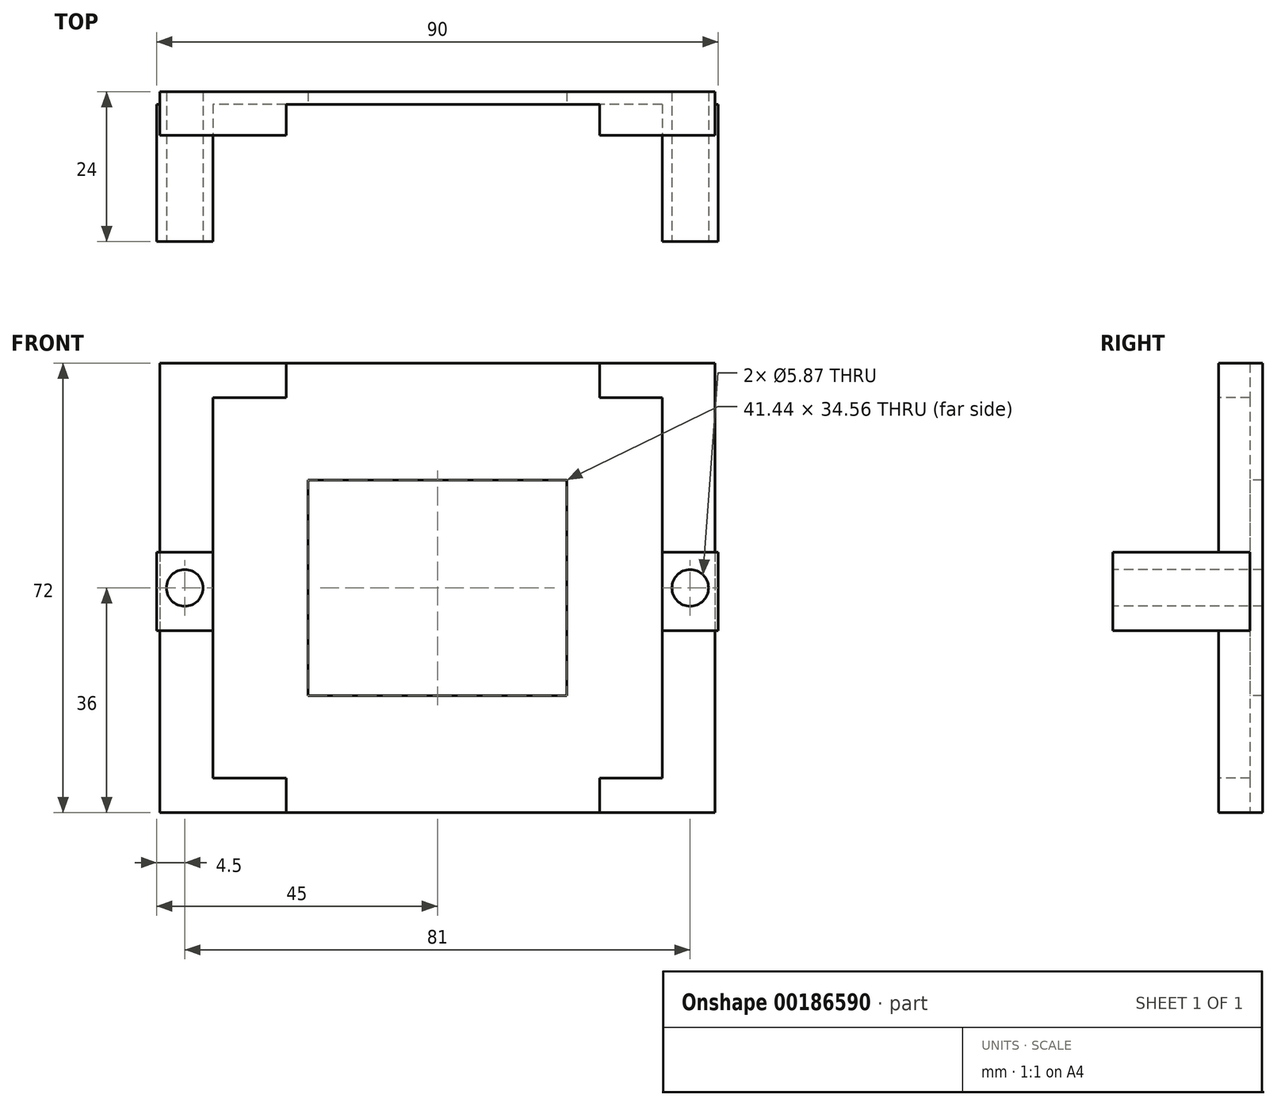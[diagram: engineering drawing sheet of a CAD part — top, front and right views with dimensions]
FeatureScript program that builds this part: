
annotation { "Feature Type Name" : "Feature", "Feature Type Description" : "" }
export const myFeature = defineFeature(function(context is Context, id is Id, definition is map)
    precondition{}
    {
        {
            var Q0;
            Q0=qCreatedBy(makeId("Front.planeOp"),FACE);
            var sketch = newSketch(context, id + "F0", { "sketchPlane" : qUnion([Q0])});
            skPoint(sketch, "E0.middle", {"position": v(0, 0) * mm});
            skLineSegment(sketch, "E1.bottom", {"start": v(44.5, 36) * mm, "end": v(-44.5, 36) * mm});
            skLineSegment(sketch, "E1.top", {"start": v(44.5, -36) * mm, "end": v(-44.5, -36) * mm});
            skLineSegment(sketch, "E1.left", {"start": v(44.5, 36) * mm, "end": v(44.5, -36) * mm});
            skLineSegment(sketch, "E1.right", {"start": v(-44.5, 36) * mm, "end": v(-44.5, -36) * mm});
            skSolve(sketch);
        }
        {
            var Q0;
            Q0 = qSketchRegion(id + "F0", true);
            extrude(context, id + "F1", {"entities" : qUnion([Q0]), "depth" : 7 * mm});
        }
        {
            var Q0;
            Q0=makeQuery(id+"F1.opExtrude","CAP_FACE",FACE,{"disambiguationData":[OSD([sQuery(id+"F0.wireOp",EDGE,"E1.bottom"),sQuery(id+"F0.wireOp",EDGE,"E1.top"),sQuery(id+"F0.wireOp",EDGE,"E1.left"),sQuery(id+"F0.wireOp",EDGE,"E1.right")])],"isStart":false});
            var sketch = newSketch(context, id + "F2", { "sketchPlane" : qUnion([Q0])});
            skLineSegment(sketch, "E2.bottom", {"start": v(36, 30.5) * mm, "end": v(-36, 30.5) * mm});
            skLineSegment(sketch, "E2.top", {"start": v(36, -30.5) * mm, "end": v(-36, -30.5) * mm});
            skLineSegment(sketch, "E2.left", {"start": v(36, 30.5) * mm, "end": v(36, -30.5) * mm});
            skLineSegment(sketch, "E2.right", {"start": v(-36, 30.5) * mm, "end": v(-36, -30.5) * mm});
            skPoint(sketch, "E2.middle", {"position": v(0, 0) * mm});
            skSolve(sketch);
        }
        {
            var Q0;
            Q0 = qSketchRegion(id + "F2", true);
            extrude(context, id + "F3", {"entities" : qUnion([Q0]), "operationType" : NewBodyOperationType.REMOVE, "oppositeDirection" : true, "depth" : 5 * mm});
        }
        {
            var Q0;
            Q0=makeQuery(id+"F3.boolean.opBoolean","COPY",FACE,{"derivedFrom":makeQuery(id+"F3.opExtrude","CAP_FACE",FACE,{"disambiguationData":[OSD([sQuery(id+"F2.wireOp",EDGE,"E2.bottom"),sQuery(id+"F2.wireOp",EDGE,"E2.top"),sQuery(id+"F2.wireOp",EDGE,"E2.left"),sQuery(id+"F2.wireOp",EDGE,"E2.right")])],"isStart":false})});
            var sketch = newSketch(context, id + "F4", { "sketchPlane" : qUnion([Q0])});
            skLineSegment(sketch, "E3.bottom", {"start": v(20.72, 17.28) * mm, "end": v(-20.72, 17.28) * mm});
            skLineSegment(sketch, "E3.top", {"start": v(20.72, -17.28) * mm, "end": v(-20.72, -17.28) * mm});
            skLineSegment(sketch, "E3.left", {"start": v(20.72, 17.28) * mm, "end": v(20.72, -17.28) * mm});
            skLineSegment(sketch, "E3.right", {"start": v(-20.72, 17.28) * mm, "end": v(-20.72, -17.28) * mm});
            skPoint(sketch, "E3.middle", {"position": v(0, 0) * mm});
            skSolve(sketch);
        }
        {
            var Q0;
            Q0 = qSketchRegion(id + "F4", true);
            extrude(context, id + "F5", {"entities" : qUnion([Q0]), "operationType" : NewBodyOperationType.REMOVE, "oppositeDirection" : true, "depth" : 25 * mm});
        }
        {
            var Q0;
            Q0=makeQuery(id+"F1.opExtrude","CAP_FACE",FACE,{"disambiguationData":[OSD([sQuery(id+"F0.wireOp",EDGE,"E1.bottom"),sQuery(id+"F0.wireOp",EDGE,"E1.top"),sQuery(id+"F0.wireOp",EDGE,"E1.left"),sQuery(id+"F0.wireOp",EDGE,"E1.right")])],"isStart":false});
            var sketch = newSketch(context, id + "F6", { "sketchPlane" : qUnion([Q0])});
            skLineSegment(sketch, "E4.bottom", {"start": v(-24.25, -30.5) * mm, "end": v(26.02, -30.5) * mm});
            skLineSegment(sketch, "E4.top", {"start": v(-24.25, -36) * mm, "end": v(26.02, -36) * mm});
            skLineSegment(sketch, "E4.left", {"start": v(-24.25, -30.5) * mm, "end": v(-24.25, -36) * mm});
            skLineSegment(sketch, "E4.right", {"start": v(26.02, -30.5) * mm, "end": v(26.02, -36) * mm});
            skLineSegment(sketch, "E5.left", {"start": v(36, 21.01) * mm, "end": v(36, -19.05) * mm});
            skLineSegment(sketch, "E5.right", {"start": v(44.5, 21.28) * mm, "end": v(44.5, -18.79) * mm});
            skPoint(sketch, "E6.firstSnap0", {"position": v(-24.25, -33.25) * mm});
            skLineSegment(sketch, "E6.bottom", {"start": v(-24.25, 36) * mm, "end": v(26.02, 36) * mm});
            skLineSegment(sketch, "E6.top", {"start": v(-24.25, 30.5) * mm, "end": v(26.02, 30.5) * mm});
            skLineSegment(sketch, "E6.left", {"start": v(-24.25, 36) * mm, "end": v(-24.25, 30.5) * mm});
            skLineSegment(sketch, "E6.right", {"start": v(26.02, 36) * mm, "end": v(26.02, 30.5) * mm});
            skSolve(sketch);
        }
        {
            var Q0;
            Q0 = qSketchRegion(id + "F6", true);
            extrude(context, id + "F7", {"entities" : qUnion([Q0]), "operationType" : NewBodyOperationType.REMOVE, "oppositeDirection" : true, "depth" : 5 * mm});
        }
        {
            var Q0;
            Q0=makeQuery(id+"F7.boolean.opBoolean","MERGE",FACE,{"derivedFrom":[makeQuery(id+"F3.boolean.opBoolean","COPY",FACE,{"derivedFrom":makeQuery(id+"F3.opExtrude","CAP_FACE",FACE,{"disambiguationData":[OSD([sQuery(id+"F2.wireOp",EDGE,"E2.bottom"),sQuery(id+"F2.wireOp",EDGE,"E2.top"),sQuery(id+"F2.wireOp",EDGE,"E2.left"),sQuery(id+"F2.wireOp",EDGE,"E2.right")])],"isStart":false})}),makeQuery(id+"F7.opExtrude","CAP_FACE",FACE,{"disambiguationData":[OSD([sQuery(id+"F6.wireOp",EDGE,"E4.bottom"),sQuery(id+"F6.wireOp",EDGE,"E4.top"),sQuery(id+"F6.wireOp",EDGE,"E4.left"),sQuery(id+"F6.wireOp",EDGE,"E4.right")])],"isStart":false}),makeQuery(id+"F7.opExtrude","CAP_FACE",FACE,{"disambiguationData":[OSD([sQuery(id+"F6.wireOp",EDGE,"E6.bottom"),sQuery(id+"F6.wireOp",EDGE,"E6.top"),sQuery(id+"F6.wireOp",EDGE,"E6.left"),sQuery(id+"F6.wireOp",EDGE,"E6.right")])],"isStart":false})]});
            var sketch = newSketch(context, id + "F8", { "sketchPlane" : qUnion([Q0])});
            skLineSegment(sketch, "E7.bottom", {"start": v(-36, -6.87) * mm, "end": v(-45, -6.87) * mm});
            skLineSegment(sketch, "E7.top", {"start": v(-36, 5.7) * mm, "end": v(-45, 5.7) * mm});
            skLineSegment(sketch, "E7.left", {"start": v(-36, -6.87) * mm, "end": v(-36, 5.7) * mm});
            skLineSegment(sketch, "E7.right", {"start": v(-45, -6.87) * mm, "end": v(-45, 5.7) * mm});
            skLineSegment(sketch, "E8.MirrorCS", {"start": v(36, 5.7) * mm, "end": v(45, 5.7) * mm});
            skLineSegment(sketch, "E9.MirrorCS", {"start": v(36, -6.87) * mm, "end": v(36, 5.7) * mm});
            skLineSegment(sketch, "E10.MirrorCS", {"start": v(36, -6.87) * mm, "end": v(45, -6.87) * mm});
            skLineSegment(sketch, "E11.MirrorCS", {"start": v(45, -6.87) * mm, "end": v(45, 5.7) * mm});
            skSolve(sketch);
        }
        {
            var Q0;
            Q0 = qSketchRegion(id + "F8", true);
            extrude(context, id + "F9", {"entities" : qUnion([Q0]), "operationType" : NewBodyOperationType.ADD, "depth" : 22 * mm});
        }
        {
            var Q0;
            Q0=makeQuery(id+"F9.opExtrude","CAP_FACE",FACE,{"disambiguationData":[OSD([sQuery(id+"F8.wireOp",EDGE,"E7.bottom"),sQuery(id+"F8.wireOp",EDGE,"E7.top"),sQuery(id+"F8.wireOp",EDGE,"E7.left"),sQuery(id+"F8.wireOp",EDGE,"E7.right")])],"isStart":false});
            var sketch = newSketch(context, id + "F10", { "sketchPlane" : qUnion([Q0])});
            skCircle(sketch, "E12", {"center": v(-40.5, 0) * mm, "radius": 2.93 * mm});
            skPoint(sketch, "E12.centerSnap0", {"position": v(-40.5, 5.7) * mm});
            skCircle(sketch, "E13.MirrorC", {"center": v(40.5, 0) * mm, "radius": 2.93 * mm});
            skSolve(sketch);
        }
        {
            var Q0;
            Q0 = qSketchRegion(id + "F10", true);
            extrude(context, id + "F11", {"entities" : qUnion([Q0]), "operationType" : NewBodyOperationType.REMOVE, "oppositeDirection" : true, "depth" : 25 * mm});
        }
    });
